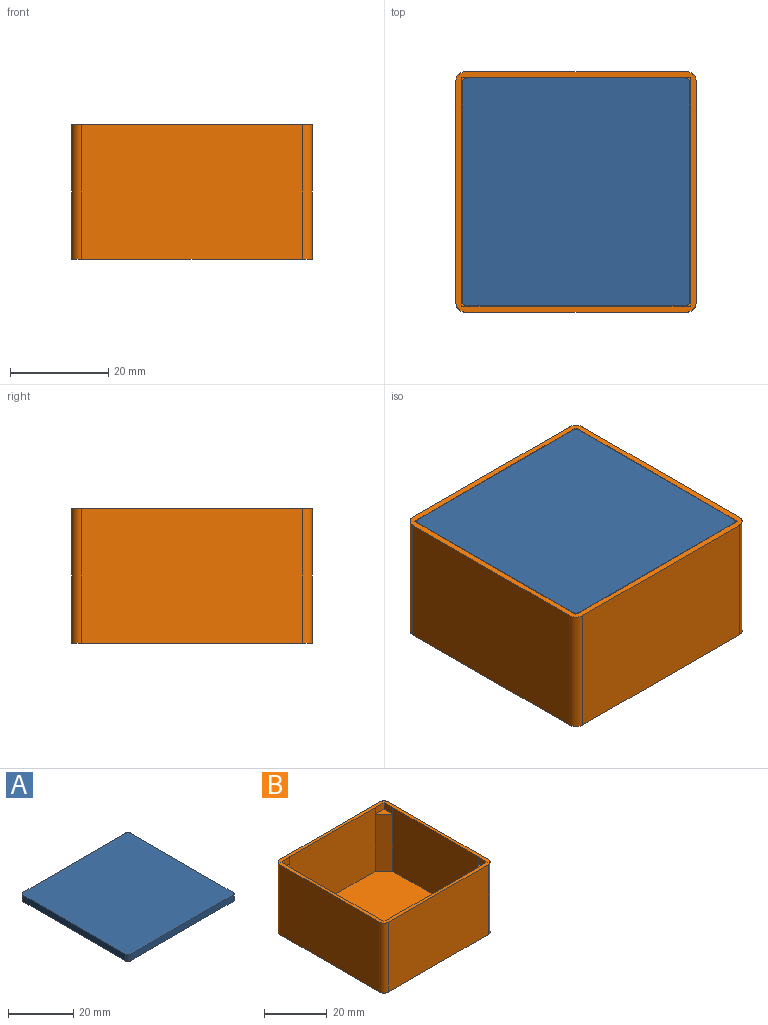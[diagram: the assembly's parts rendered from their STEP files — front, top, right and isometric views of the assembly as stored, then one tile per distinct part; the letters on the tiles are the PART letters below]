
ASSEMBLY  parts=2 mates=1
PART A: 10 faces, bbox 46.4x46.4x2.4 mm
  f0: plane 44.4x2.4mm, normal (0,1,0), area 106.6mm2, adj f4,f5,f6,f9
  f1: plane 44.4x2.4mm, normal (-1,0,0), area 106.6mm2, adj f4,f5,f6,f7
  f2: plane 44.4x2.4mm, normal (0,-1,0), area 106.6mm2, adj f4,f5,f7,f8
  f3: plane 44.4x2.4mm, normal (1,0,0), area 106.6mm2, adj f4,f5,f8,f9
  f4: plane 46.4x46.4mm, normal (0,0,1), area 2152.1mm2, adj f0,f1,f2,f3,f6,f7,f8,f9
  f5: plane 46.4x46.4mm, normal (0,0,-1), area 2152.1mm2, adj f0,f1,f2,f3,f6,f7,f8,f9
  f6: cylinder r=1mm len=2.4mm, axis (0,0,1), area 3.8mm2, adj f0,f1,f4,f5
  f7: cylinder r=1mm len=2.4mm, axis (0,0,-1), area 3.8mm2, adj f1,f2,f4,f5
  f8: cylinder r=1mm len=2.4mm, axis (0,0,1), area 3.8mm2, adj f2,f3,f4,f5
  f9: cylinder r=1mm len=2.4mm, axis (0,0,-1), area 3.8mm2, adj f0,f3,f4,f5
PART B: 31 faces, bbox 49x49x27.3 mm
  f0: plane 49x49mm, normal (0,0,1), area 227.6mm2, adj f1,f2,f3,f4,f5,f6,f8,f9
  f1: plane 24.9x4mm, normal (-0.71,-0.71,0), area 126.5mm2, adj f0,f8,f9,f12,f25,f26,f27
  f2: plane 24.9x4mm, normal (-0.71,0.71,0), area 126.5mm2, adj f0,f8,f11,f12,f19,f20,f21
  f3: plane 45x27.3mm, normal (0,1,0), area 1228.5mm2, adj f0,f7,f13,f16
  f4: plane 45x27.3mm, normal (-1,0,0), area 1228.5mm2, adj f0,f7,f13,f14
  f5: plane 45x27.3mm, normal (0,-1,0), area 1228.5mm2, adj f0,f7,f14,f15
  f6: plane 45x27.3mm, normal (1,0,0), area 1228.5mm2, adj f0,f7,f15,f16
  f7: plane 49x49mm, normal (0,0,-1), area 2397.6mm2, adj f3,f4,f5,f6,f13,f14,f15,f16
  f8: plane 38.6x24.9mm, normal (-1,0,0), area 961.1mm2, adj f0,f1,f2,f12
  f9: plane 38.6x24.9mm, normal (0,-1,0), area 961.1mm2, adj f0,f1,f12,f17
  f10: plane 38.6x24.9mm, normal (1,0,0), area 961.1mm2, adj f0,f12,f17,f18
  f11: plane 38.6x24.9mm, normal (0,1,0), area 961.1mm2, adj f0,f2,f12,f18
  f12: plane 46.6x46.6mm, normal (0,0,1), area 2139.6mm2, adj f1,f2,f8,f9,f10,f11,f17,f18
  f13: cylinder r=2mm len=27.3mm, axis (0,0,1), area 85.8mm2, adj f0,f3,f4,f7
  f14: cylinder r=2mm len=27.3mm, axis (0,0,-1), area 85.8mm2, adj f0,f4,f5,f7
  f15: cylinder r=2mm len=27.3mm, axis (0,0,1), area 85.8mm2, adj f0,f5,f6,f7
  f16: cylinder r=2mm len=27.3mm, axis (0,0,-1), area 85.8mm2, adj f0,f3,f6,f7
  f17: plane 24.9x4mm, normal (0.71,-0.71,0), area 126.5mm2, adj f0,f9,f10,f12,f28,f29,f30
  f18: plane 24.9x4mm, normal (0.71,0.71,0), area 126.5mm2, adj f0,f10,f11,f12,f22,f23,f24
  f19: plane 3.9x3.9mm, normal (0,0,1), area 7.6mm2, adj f2,f20,f21
  f20: plane 3.9x2.6mm, normal (0,1,0), area 10.1mm2, adj f0,f2,f19,f21
  f21: plane 3.9x2.6mm, normal (-1,0,0), area 10.1mm2, adj f0,f2,f19,f20
  f22: plane 3.9x3.9mm, normal (0,0,1), area 7.6mm2, adj f18,f23,f24
  f23: plane 3.9x2.6mm, normal (0,1,0), area 10.1mm2, adj f0,f18,f22,f24
  f24: plane 3.9x2.6mm, normal (1,0,0), area 10.1mm2, adj f0,f18,f22,f23
  f25: plane 3.9x3.9mm, normal (0,0,1), area 7.6mm2, adj f1,f26,f27
  f26: plane 3.9x2.6mm, normal (0,-1,0), area 10.1mm2, adj f0,f1,f25,f27
  f27: plane 3.9x2.6mm, normal (-1,0,0), area 10.1mm2, adj f0,f1,f25,f26
  f28: plane 3.9x2.6mm, normal (0,-1,0), area 10.1mm2, adj f0,f17,f29,f30
  f29: plane 3.9x2.6mm, normal (1,0,0), area 10.1mm2, adj f0,f17,f28,f30
  f30: plane 3.9x3.9mm, normal (0,0,1), area 7.6mm2, adj f17,f28,f29
PLACE A t=(-75.53,-3.15,24.9)mm
PLACE B at identity fixed
MATE slider B.f12 <-> A.f4  axis (0,0,1) through (-41.84,40.26,2.4)mm
